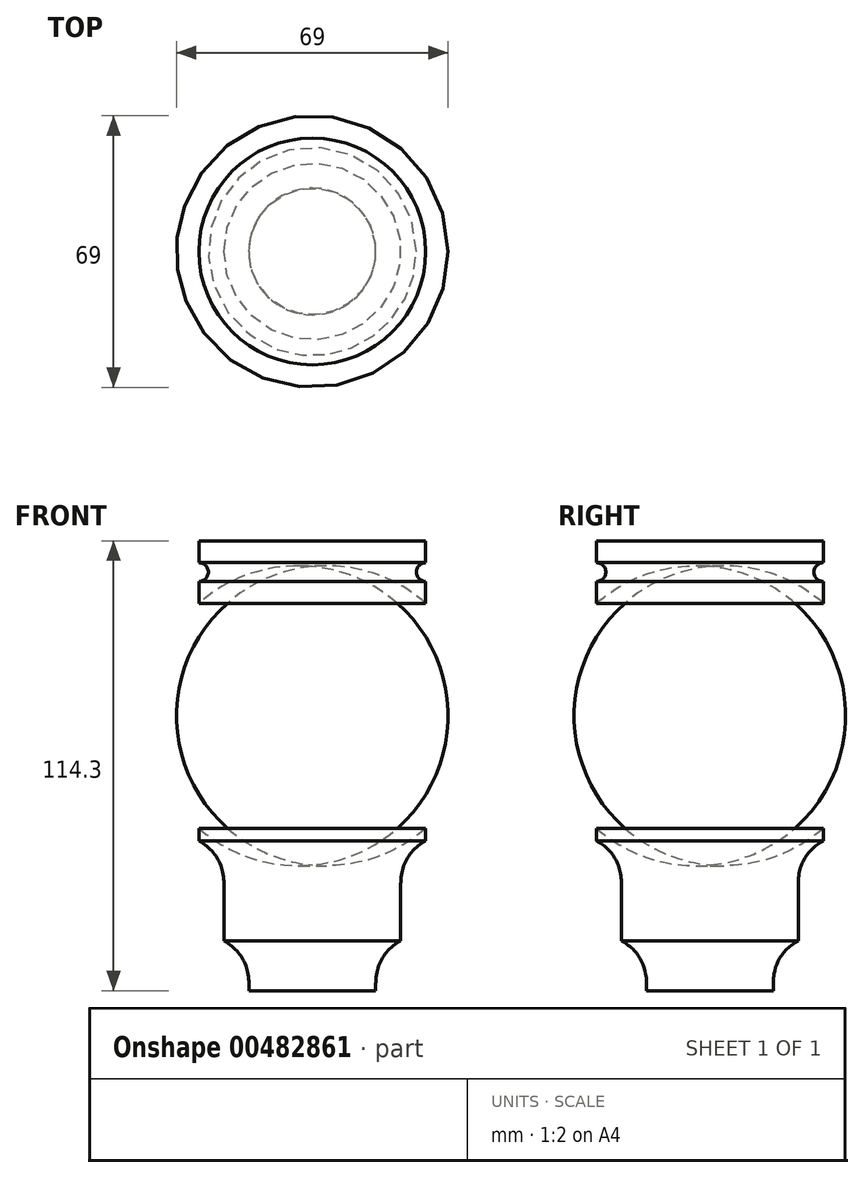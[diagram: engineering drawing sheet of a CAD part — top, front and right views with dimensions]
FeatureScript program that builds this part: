
annotation { "Feature Type Name" : "Feature", "Feature Type Description" : "" }
export const myFeature = defineFeature(function(context is Context, id is Id, definition is map)
    precondition{}
    {
        {
            var Q0;
            Q0=qCreatedBy(makeId("Front.planeOp"),FACE);
            var sketch = newSketch(context, id + "F0", { "sketchPlane" : qUnion([Q0])});
            skLineSegment(sketch, "E0", {"start": v(0, 0) * mm, "end": v(0, 114.3) * mm});
            skLineSegment(sketch, "E1", {"start": v(0, 114.3) * mm, "end": v(28.8, 114.3) * mm});
            skLineSegment(sketch, "E2", {"start": v(28.8, 114.3) * mm, "end": v(28.8, 98.43) * mm});
            skArc(sketch, "E3", {"start": v(28.8, 41.28) * mm, "mid": v(41.7, 69.85) * mm, "end": v(28.8, 98.43) * mm});
            skLineSegment(sketch, "E4", {"start": v(0, 0) * mm, "end": v(16.1, 0) * mm});
            skLineSegment(sketch, "E5", {"start": v(16.1, 0) * mm, "end": v(16.1, 12.7) * mm});
            skLineSegment(sketch, "E6", {"start": v(16.1, 12.7) * mm, "end": v(22.45, 12.7) * mm});
            skLineSegment(sketch, "E7", {"start": v(22.45, 12.7) * mm, "end": v(22.45, 38.1) * mm});
            skLineSegment(sketch, "E8", {"start": v(22.45, 38.1) * mm, "end": v(28.8, 38.1) * mm});
            skLineSegment(sketch, "E9", {"start": v(28.8, 38.1) * mm, "end": v(28.8, 41.27) * mm});
            skSolve(sketch);
        }
        {
            var Q0;
            Q0=qCreatedBy(makeId("Front.planeOp"),FACE);
            var sketch = newSketch(context, id + "F1", { "sketchPlane" : qUnion([Q0])});
            skLineSegment(sketch, "E10.0", {"start": v(28.8, 114.3) * mm, "end": v(28.8, 98.43) * mm, "construction": true});
            skLineSegment(sketch, "E11.0", {"start": v(22.45, 12.7) * mm, "end": v(22.45, 38.1) * mm, "construction": true});
            skArc(sketch, "E12", {"start": v(28.8, 108.74) * mm, "mid": v(26.42, 106.36) * mm, "end": v(28.8, 103.98) * mm, "construction": true});
            skArc(sketch, "E13", {"start": v(22.45, 14.29) * mm, "mid": v(27.22, 19.05) * mm, "end": v(22.45, 23.81) * mm});
            skLineSegment(sketch, "E14", {"start": v(0, 0) * mm, "end": v(0, 103.81) * mm, "construction": true});
            skLineSegment(sketch, "E15", {"start": v(28.8, 108.74) * mm, "end": v(28.8, 103.98) * mm});
            skLineSegment(sketch, "E16", {"start": v(22.45, 23.81) * mm, "end": v(22.45, 14.29) * mm});
            skSolve(sketch);
        }
        {
            var Q0;
            Q0=qCreatedBy(makeId("Front.planeOp"),FACE);
            var sketch = newSketch(context, id + "F2", { "sketchPlane" : qUnion([Q0])});
            skArc(sketch, "E17.0", {"start": v(28.8, 108.74) * mm, "mid": v(26.42, 106.36) * mm, "end": v(28.8, 103.98) * mm});
            skLineSegment(sketch, "E18.0", {"start": v(28.8, 108.74) * mm, "end": v(28.8, 103.98) * mm});
            skSolve(sketch);
        }
        {
            var Q0;
            Q0 = qSketchRegion(id + "F0", true);
            var Q1;
            Q1=sQuery(id+"F0.wireOp",EDGE,"E0");
            revolve(context, id + "F3", {"entities" : qUnion([Q0]), "axis" : qUnion([Q1]), "revolveType" : RevolveType.FULL});
        }
        {
            var Q0;
            Q0=makeQuery(id+"F3.opRevolve","SWEPT_EDGE",EDGE,{"disambiguationData":[OSD([sQuery(id+"F0.wireOp",EDGE,"E7"),sQuery(id+"F0.wireOp",EDGE,"E8")])]});
            var Q1;
            Q1=makeQuery(id+"F3.opRevolve","SWEPT_EDGE",EDGE,{"disambiguationData":[OSD([sQuery(id+"F0.wireOp",EDGE,"E5"),sQuery(id+"F0.wireOp",EDGE,"E6")])]});
            fillet(context, id + "F4", {"entities" : qUnion([Q0, Q1]), "radius" : 12.7 * mm, "tangentPropagation" : true, "rho" : .5, "crossSection" : FilletCrossSection.CONIC, "allowEdgeOverflow" : false});
        }
        {
            var Q0;
            Q0=sQuery(id+"F1.wireOp",EDGE,"E13");
            var Q1;
            Q1=sQuery(id+"F1.wireOp",EDGE,"E14");
            revolve(context, id + "F5", {"bodyType" : ToolBodyType.SURFACE, "surfaceEntities" : qUnion([Q0]), "axis" : qUnion([Q1]), "revolveType" : RevolveType.FULL});
        }
        {
            var Q0;
            Q0 = qSketchRegion(id + "F2", true);
            var Q1;
            Q1=sQuery(id+"F1.wireOp",EDGE,"E14");
            revolve(context, id + "F6", {"operationType" : NewBodyOperationType.REMOVE, "entities" : qUnion([Q0]), "axis" : qUnion([Q1]), "revolveType" : RevolveType.FULL, "oppositeDirection" : true});
        }
    });
